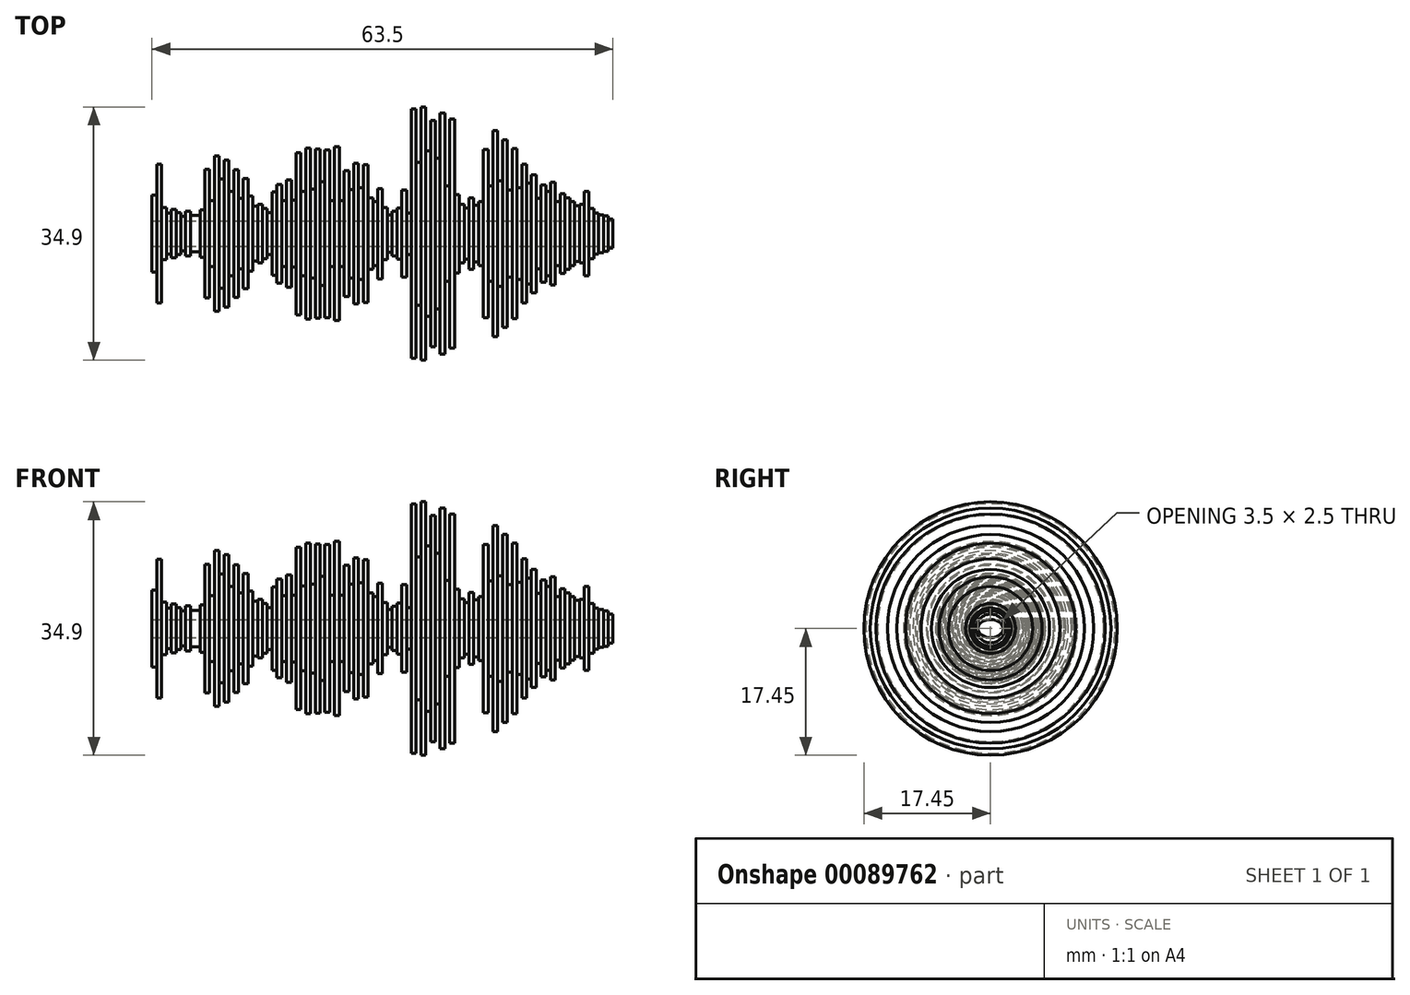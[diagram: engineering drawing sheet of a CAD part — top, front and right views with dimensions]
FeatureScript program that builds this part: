
annotation { "Feature Type Name" : "Feature", "Feature Type Description" : "" }
export const myFeature = defineFeature(function(context is Context, id is Id, definition is map)
    precondition{}
    {
        {
            var Q0;
            Q0=qCreatedBy(makeId("Front.planeOp"),FACE);
            var sketch = newSketch(context, id + "F0", { "sketchPlane" : qUnion([Q0])});
            skLineSegment(sketch, "E0", {"start": v(-31.75, 0) * mm, "end": v(31.75, 0) * mm});
            skLineSegment(sketch, "E1", {"start": v(-31.75, 0) * mm, "end": v(-31.75, 5.3) * mm});
            skLineSegment(sketch, "E2", {"start": v(-31.75, 5.3) * mm, "end": v(-31.09, 5.3) * mm});
            skLineSegment(sketch, "E3", {"start": v(-31.09, 9.56) * mm, "end": v(-30.43, 9.56) * mm});
            skLineSegment(sketch, "E4", {"start": v(-30.43, 3.61) * mm, "end": v(-29.77, 3.61) * mm});
            skLineSegment(sketch, "E5", {"start": v(-29.77, 2.8) * mm, "end": v(-29.1, 2.8) * mm});
            skLineSegment(sketch, "E6", {"start": v(-29.1, 3.36) * mm, "end": v(-28.44, 3.36) * mm});
            skLineSegment(sketch, "E7", {"start": v(-28.44, 2.9) * mm, "end": v(-27.78, 2.9) * mm});
            skLineSegment(sketch, "E8", {"start": v(-27.78, 2.4) * mm, "end": v(-27.12, 2.4) * mm});
            skLineSegment(sketch, "E9", {"start": v(-27.12, 3.1) * mm, "end": v(-26.46, 3.1) * mm});
            skLineSegment(sketch, "E10", {"start": v(-26.46, 2.52) * mm, "end": v(-25.8, 2.52) * mm});
            skLineSegment(sketch, "E11", {"start": v(-25.8, 2.52) * mm, "end": v(-25.14, 2.52) * mm});
            skLineSegment(sketch, "E12", {"start": v(-25.14, 3.27) * mm, "end": v(-24.47, 3.27) * mm});
            skLineSegment(sketch, "E13", {"start": v(-23.81, 4.52) * mm, "end": v(-23.15, 4.52) * mm});
            skLineSegment(sketch, "E14", {"start": v(-23.15, 10.72) * mm, "end": v(-22.49, 10.72) * mm});
            skLineSegment(sketch, "E15", {"start": v(-22.49, 7.5) * mm, "end": v(-21.83, 7.5) * mm});
            skLineSegment(sketch, "E16", {"start": v(-21.83, 10.16) * mm, "end": v(-21.17, 10.16) * mm});
            skLineSegment(sketch, "E17", {"start": v(-21.17, 5.8) * mm, "end": v(-20.5, 5.8) * mm});
            skLineSegment(sketch, "E18", {"start": v(-20.5, 8.8) * mm, "end": v(-19.84, 8.8) * mm});
            skLineSegment(sketch, "E19", {"start": v(-19.84, 4.88) * mm, "end": v(-19.18, 4.88) * mm});
            skLineSegment(sketch, "E20", {"start": v(-19.18, 7.6) * mm, "end": v(-18.52, 7.6) * mm});
            skLineSegment(sketch, "E21", {"start": v(-18.52, 5.19) * mm, "end": v(-17.86, 5.19) * mm});
            skLineSegment(sketch, "E22", {"start": v(-17.86, 3.79) * mm, "end": v(-17.2, 3.79) * mm});
            skLineSegment(sketch, "E23", {"start": v(-17.2, 4.02) * mm, "end": v(-16.54, 4.02) * mm});
            skLineSegment(sketch, "E24", {"start": v(-16.54, 3.44) * mm, "end": v(-15.88, 3.44) * mm});
            skLineSegment(sketch, "E25", {"start": v(-15.88, 2.87) * mm, "end": v(-15.21, 2.87) * mm});
            skLineSegment(sketch, "E26", {"start": v(-15.21, 5.73) * mm, "end": v(-14.55, 5.73) * mm});
            skLineSegment(sketch, "E27", {"start": v(-31.09, 5.3) * mm, "end": v(-31.09, 9.56) * mm});
            skLineSegment(sketch, "E28", {"start": v(-30.43, 9.56) * mm, "end": v(-30.43, 3.61) * mm});
            skLineSegment(sketch, "E29", {"start": v(-29.77, 3.61) * mm, "end": v(-29.77, 2.8) * mm});
            skLineSegment(sketch, "E30", {"start": v(-29.1, 3.36) * mm, "end": v(-29.1, 2.8) * mm});
            skLineSegment(sketch, "E31", {"start": v(-28.44, 3.36) * mm, "end": v(-28.44, 2.9) * mm});
            skLineSegment(sketch, "E32", {"start": v(-27.78, 2.9) * mm, "end": v(-27.78, 2.4) * mm});
            skLineSegment(sketch, "E33", {"start": v(-27.12, 2.4) * mm, "end": v(-27.12, 3.1) * mm});
            skLineSegment(sketch, "E34", {"start": v(-26.46, 3.1) * mm, "end": v(-26.46, 2.52) * mm});
            skLineSegment(sketch, "E35", {"start": v(-25.14, 2.52) * mm, "end": v(-25.14, 3.27) * mm});
            skLineSegment(sketch, "E36", {"start": v(-24.47, 3.27) * mm, "end": v(-24.47, 8.86) * mm});
            skLineSegment(sketch, "E37", {"start": v(-24.47, 8.86) * mm, "end": v(-23.81, 8.86) * mm});
            skLineSegment(sketch, "E38", {"start": v(-23.81, 8.86) * mm, "end": v(-23.81, 4.52) * mm});
            skLineSegment(sketch, "E39", {"start": v(-23.15, 4.52) * mm, "end": v(-23.15, 10.72) * mm});
            skLineSegment(sketch, "E40", {"start": v(-22.49, 10.72) * mm, "end": v(-22.49, 7.5) * mm});
            skLineSegment(sketch, "E41", {"start": v(-21.83, 7.5) * mm, "end": v(-21.83, 10.16) * mm});
            skLineSegment(sketch, "E42", {"start": v(-21.17, 10.16) * mm, "end": v(-21.17, 5.8) * mm});
            skLineSegment(sketch, "E43", {"start": v(-20.5, 5.8) * mm, "end": v(-20.5, 8.8) * mm});
            skLineSegment(sketch, "E44", {"start": v(-19.84, 8.8) * mm, "end": v(-19.84, 4.88) * mm});
            skLineSegment(sketch, "E45", {"start": v(-19.18, 4.88) * mm, "end": v(-19.18, 7.6) * mm});
            skLineSegment(sketch, "E46", {"start": v(-18.52, 7.6) * mm, "end": v(-18.52, 5.19) * mm});
            skLineSegment(sketch, "E47", {"start": v(-17.86, 3.79) * mm, "end": v(-17.86, 5.19) * mm});
            skLineSegment(sketch, "E48", {"start": v(-17.2, 4.02) * mm, "end": v(-17.2, 3.79) * mm});
            skLineSegment(sketch, "E49", {"start": v(-16.54, 3.44) * mm, "end": v(-16.54, 4.02) * mm});
            skLineSegment(sketch, "E50", {"start": v(-15.88, 3.44) * mm, "end": v(-15.88, 2.87) * mm});
            skLineSegment(sketch, "E51", {"start": v(-15.21, 2.87) * mm, "end": v(-15.21, 5.73) * mm});
            skLineSegment(sketch, "E52", {"start": v(-14.55, 6.8) * mm, "end": v(-14.55, 5.73) * mm});
            skLineSegment(sketch, "E53", {"start": v(-14.55, 6.8) * mm, "end": v(-13.9, 6.8) * mm});
            skLineSegment(sketch, "E54", {"start": v(-13.9, 4.56) * mm, "end": v(-13.23, 4.56) * mm});
            skLineSegment(sketch, "E55", {"start": v(-13.23, 7.4) * mm, "end": v(-12.57, 7.4) * mm});
            skLineSegment(sketch, "E56", {"start": v(-12.57, 4.59) * mm, "end": v(-11.9, 4.59) * mm});
            skLineSegment(sketch, "E57", {"start": v(-11.9, 11.17) * mm, "end": v(-11.24, 11.17) * mm});
            skLineSegment(sketch, "E58", {"start": v(-11.24, 5.84) * mm, "end": v(-10.58, 5.84) * mm});
            skLineSegment(sketch, "E59", {"start": v(-10.58, 11.76) * mm, "end": v(-9.92, 11.76) * mm});
            skLineSegment(sketch, "E60", {"start": v(-9.92, 6.14) * mm, "end": v(-9.26, 6.14) * mm});
            skLineSegment(sketch, "E61", {"start": v(-9.26, 11.66) * mm, "end": v(-8.6, 11.66) * mm});
            skLineSegment(sketch, "E62", {"start": v(-8.6, 7.17) * mm, "end": v(-7.94, 7.17) * mm});
            skLineSegment(sketch, "E63", {"start": v(-7.94, 11.56) * mm, "end": v(-7.28, 11.56) * mm});
            skLineSegment(sketch, "E64", {"start": v(-7.28, 4.56) * mm, "end": v(-6.61, 4.56) * mm});
            skLineSegment(sketch, "E65", {"start": v(-6.61, 12) * mm, "end": v(-5.95, 12) * mm});
            skLineSegment(sketch, "E66", {"start": v(-5.95, 4.56) * mm, "end": v(-5.3, 4.56) * mm});
            skLineSegment(sketch, "E67", {"start": v(-13.9, 6.8) * mm, "end": v(-13.9, 4.56) * mm});
            skLineSegment(sketch, "E68", {"start": v(-13.23, 7.4) * mm, "end": v(-13.23, 4.56) * mm});
            skLineSegment(sketch, "E69", {"start": v(-12.57, 7.4) * mm, "end": v(-12.57, 4.59) * mm});
            skLineSegment(sketch, "E70", {"start": v(-11.9, 11.17) * mm, "end": v(-11.9, 4.59) * mm});
            skLineSegment(sketch, "E71", {"start": v(-11.24, 11.17) * mm, "end": v(-11.24, 5.84) * mm});
            skLineSegment(sketch, "E72", {"start": v(-10.58, 11.76) * mm, "end": v(-10.58, 5.84) * mm});
            skLineSegment(sketch, "E73", {"start": v(-9.92, 11.76) * mm, "end": v(-9.92, 6.14) * mm});
            skLineSegment(sketch, "E74", {"start": v(-9.26, 11.66) * mm, "end": v(-9.26, 6.14) * mm});
            skLineSegment(sketch, "E75", {"start": v(-8.6, 11.66) * mm, "end": v(-8.6, 7.17) * mm});
            skLineSegment(sketch, "E76", {"start": v(-7.94, 11.56) * mm, "end": v(-7.94, 7.17) * mm});
            skLineSegment(sketch, "E77", {"start": v(-7.28, 11.56) * mm, "end": v(-7.28, 4.56) * mm});
            skLineSegment(sketch, "E78", {"start": v(-6.61, 4.56) * mm, "end": v(-6.61, 12) * mm});
            skLineSegment(sketch, "E79", {"start": v(-5.95, 12) * mm, "end": v(-5.95, 4.56) * mm});
            skLineSegment(sketch, "E80", {"start": v(-5.3, 8.69) * mm, "end": v(-4.63, 8.69) * mm});
            skLineSegment(sketch, "E81", {"start": v(-4.63, 6.1) * mm, "end": v(-3.97, 6.1) * mm});
            skLineSegment(sketch, "E82", {"start": v(-3.97, 9.7) * mm, "end": v(-3.3, 9.7) * mm});
            skLineSegment(sketch, "E83", {"start": v(-3.3, 6.33) * mm, "end": v(-2.65, 6.33) * mm});
            skLineSegment(sketch, "E84", {"start": v(-2.65, 9.47) * mm, "end": v(-1.98, 9.47) * mm});
            skLineSegment(sketch, "E85", {"start": v(-1.98, 4.9) * mm, "end": v(-1.32, 4.9) * mm});
            skLineSegment(sketch, "E86", {"start": v(-1.32, 4.4) * mm, "end": v(-0.66, 4.4) * mm});
            skLineSegment(sketch, "E87", {"start": v(-0.66, 6.23) * mm, "end": v(0, 6.23) * mm});
            skLineSegment(sketch, "E88", {"start": v(0, 3.6) * mm, "end": v(0.66, 3.6) * mm});
            skLineSegment(sketch, "E89", {"start": v(0.66, 2.6) * mm, "end": v(1.32, 2.6) * mm});
            skLineSegment(sketch, "E90", {"start": v(1.32, 3.06) * mm, "end": v(1.98, 3.06) * mm});
            skLineSegment(sketch, "E91", {"start": v(1.98, 3.53) * mm, "end": v(2.65, 3.53) * mm});
            skLineSegment(sketch, "E92", {"start": v(2.65, 6.02) * mm, "end": v(3.3, 6.02) * mm});
            skLineSegment(sketch, "E93", {"start": v(3.3, 2.86) * mm, "end": v(3.97, 2.86) * mm});
            skLineSegment(sketch, "E94", {"start": v(3.97, 17.17) * mm, "end": v(4.63, 17.17) * mm});
            skLineSegment(sketch, "E95", {"start": v(4.63, 9.84) * mm, "end": v(5.3, 9.84) * mm});
            skLineSegment(sketch, "E96", {"start": v(5.3, 17.45) * mm, "end": v(5.95, 17.45) * mm});
            skLineSegment(sketch, "E97", {"start": v(5.95, 11.39) * mm, "end": v(6.61, 11.39) * mm});
            skLineSegment(sketch, "E98", {"start": v(6.61, 15.58) * mm, "end": v(7.28, 15.58) * mm});
            skLineSegment(sketch, "E99", {"start": v(7.28, 10.37) * mm, "end": v(7.94, 10.37) * mm});
            skLineSegment(sketch, "E100", {"start": v(7.94, 16.59) * mm, "end": v(8.6, 16.59) * mm});
            skLineSegment(sketch, "E101", {"start": v(8.6, 6.6) * mm, "end": v(9.26, 6.6) * mm});
            skLineSegment(sketch, "E102", {"start": v(9.26, 15.79) * mm, "end": v(9.92, 15.79) * mm});
            skLineSegment(sketch, "E103", {"start": v(9.92, 5.4) * mm, "end": v(10.58, 5.4) * mm});
            skLineSegment(sketch, "E104", {"start": v(10.58, 4.06) * mm, "end": v(11.24, 4.06) * mm});
            skLineSegment(sketch, "E105", {"start": v(11.24, 3.55) * mm, "end": v(11.9, 3.55) * mm});
            skLineSegment(sketch, "E106", {"start": v(11.9, 4.95) * mm, "end": v(12.57, 4.95) * mm});
            skLineSegment(sketch, "E107", {"start": v(12.57, 3.93) * mm, "end": v(13.23, 3.93) * mm});
            skLineSegment(sketch, "E108", {"start": v(13.23, 4.4) * mm, "end": v(13.9, 4.4) * mm});
            skLineSegment(sketch, "E109", {"start": v(13.9, 11.6) * mm, "end": v(14.55, 11.6) * mm});
            skLineSegment(sketch, "E110", {"start": v(14.55, 6.56) * mm, "end": v(15.21, 6.56) * mm});
            skLineSegment(sketch, "E111", {"start": v(15.21, 14.2) * mm, "end": v(15.88, 14.2) * mm});
            skLineSegment(sketch, "E112", {"start": v(-4.63, 6.1) * mm, "end": v(-4.63, 8.69) * mm});
            skLineSegment(sketch, "E113", {"start": v(-3.97, 9.7) * mm, "end": v(-3.97, 6.1) * mm});
            skLineSegment(sketch, "E114", {"start": v(-3.3, 9.7) * mm, "end": v(-3.3, 6.33) * mm});
            skLineSegment(sketch, "E115", {"start": v(-2.65, 9.47) * mm, "end": v(-2.65, 6.33) * mm});
            skLineSegment(sketch, "E116", {"start": v(-1.98, 4.9) * mm, "end": v(-1.98, 9.47) * mm});
            skLineSegment(sketch, "E117", {"start": v(-1.32, 4.4) * mm, "end": v(-1.32, 4.9) * mm});
            skLineSegment(sketch, "E118", {"start": v(-0.66, 4.4) * mm, "end": v(-0.66, 6.23) * mm});
            skLineSegment(sketch, "E119", {"start": v(0, 6.23) * mm, "end": v(0, 3.6) * mm});
            skLineSegment(sketch, "E120", {"start": v(0.66, 2.6) * mm, "end": v(0.66, 3.6) * mm});
            skLineSegment(sketch, "E121", {"start": v(1.32, 2.6) * mm, "end": v(1.32, 3.06) * mm});
            skLineSegment(sketch, "E122", {"start": v(1.98, 3.06) * mm, "end": v(1.98, 3.53) * mm});
            skLineSegment(sketch, "E123", {"start": v(2.65, 3.53) * mm, "end": v(2.65, 6.02) * mm});
            skLineSegment(sketch, "E124", {"start": v(3.3, 2.86) * mm, "end": v(3.3, 6.02) * mm});
            skLineSegment(sketch, "E125", {"start": v(3.97, 2.86) * mm, "end": v(3.97, 17.17) * mm});
            skLineSegment(sketch, "E126", {"start": v(4.63, 9.84) * mm, "end": v(4.63, 17.17) * mm});
            skLineSegment(sketch, "E127", {"start": v(5.3, 9.84) * mm, "end": v(5.3, 17.45) * mm});
            skLineSegment(sketch, "E128", {"start": v(5.95, 11.39) * mm, "end": v(5.95, 17.45) * mm});
            skLineSegment(sketch, "E129", {"start": v(7.28, 10.37) * mm, "end": v(7.28, 15.58) * mm});
            skLineSegment(sketch, "E130", {"start": v(7.94, 10.37) * mm, "end": v(7.94, 16.59) * mm});
            skLineSegment(sketch, "E131", {"start": v(8.6, 6.6) * mm, "end": v(8.6, 16.59) * mm});
            skLineSegment(sketch, "E132", {"start": v(9.26, 15.79) * mm, "end": v(9.26, 6.6) * mm});
            skLineSegment(sketch, "E133", {"start": v(9.92, 15.79) * mm, "end": v(9.92, 5.4) * mm});
            skLineSegment(sketch, "E134", {"start": v(11.24, 3.55) * mm, "end": v(11.24, 4.06) * mm});
            skLineSegment(sketch, "E135", {"start": v(11.9, 3.55) * mm, "end": v(11.9, 4.95) * mm});
            skLineSegment(sketch, "E136", {"start": v(12.57, 3.93) * mm, "end": v(12.57, 4.95) * mm});
            skLineSegment(sketch, "E137", {"start": v(13.23, 3.93) * mm, "end": v(13.23, 4.4) * mm});
            skLineSegment(sketch, "E138", {"start": v(13.9, 4.4) * mm, "end": v(13.9, 11.6) * mm});
            skLineSegment(sketch, "E139", {"start": v(14.55, 6.56) * mm, "end": v(14.55, 11.6) * mm});
            skLineSegment(sketch, "E140", {"start": v(15.21, 6.56) * mm, "end": v(15.21, 14.2) * mm});
            skLineSegment(sketch, "E141", {"start": v(15.88, 7.28) * mm, "end": v(16.54, 7.28) * mm});
            skLineSegment(sketch, "E142", {"start": v(16.54, 12.94) * mm, "end": v(17.2, 12.94) * mm});
            skLineSegment(sketch, "E143", {"start": v(17.2, 6.02) * mm, "end": v(17.86, 6.02) * mm});
            skLineSegment(sketch, "E144", {"start": v(17.86, 11.74) * mm, "end": v(18.52, 11.74) * mm});
            skLineSegment(sketch, "E145", {"start": v(18.52, 6.34) * mm, "end": v(19.18, 6.34) * mm});
            skLineSegment(sketch, "E146", {"start": v(19.18, 9.58) * mm, "end": v(19.84, 9.58) * mm});
            skLineSegment(sketch, "E147", {"start": v(19.84, 6.94) * mm, "end": v(20.5, 6.94) * mm});
            skLineSegment(sketch, "E148", {"start": v(20.5, 8.12) * mm, "end": v(21.17, 8.12) * mm});
            skLineSegment(sketch, "E149", {"start": v(21.17, 4.83) * mm, "end": v(21.83, 4.83) * mm});
            skLineSegment(sketch, "E150", {"start": v(21.83, 6.67) * mm, "end": v(22.49, 6.67) * mm});
            skLineSegment(sketch, "E151", {"start": v(22.49, 5.8) * mm, "end": v(23.15, 5.8) * mm});
            skLineSegment(sketch, "E152", {"start": v(23.15, 7.1) * mm, "end": v(23.81, 7.1) * mm});
            skLineSegment(sketch, "E153", {"start": v(23.81, 4.39) * mm, "end": v(24.47, 4.39) * mm});
            skLineSegment(sketch, "E154", {"start": v(24.47, 5.47) * mm, "end": v(25.14, 5.47) * mm});
            skLineSegment(sketch, "E155", {"start": v(25.14, 4.9) * mm, "end": v(25.8, 4.9) * mm});
            skLineSegment(sketch, "E156", {"start": v(25.8, 4.39) * mm, "end": v(26.46, 4.39) * mm});
            skLineSegment(sketch, "E157", {"start": v(26.46, 3.87) * mm, "end": v(27.12, 3.87) * mm});
            skLineSegment(sketch, "E158", {"start": v(27.12, 4.03) * mm, "end": v(27.78, 4.03) * mm});
            skLineSegment(sketch, "E159", {"start": v(27.78, 5.8) * mm, "end": v(28.44, 5.8) * mm});
            skLineSegment(sketch, "E160", {"start": v(28.44, 3.43) * mm, "end": v(29.1, 3.43) * mm});
            skLineSegment(sketch, "E161", {"start": v(29.1, 2.83) * mm, "end": v(29.77, 2.83) * mm});
            skLineSegment(sketch, "E162", {"start": v(29.77, 2.6) * mm, "end": v(30.43, 2.6) * mm});
            skLineSegment(sketch, "E163", {"start": v(30.43, 2.45) * mm, "end": v(31.09, 2.45) * mm});
            skLineSegment(sketch, "E164", {"start": v(31.09, 1.99) * mm, "end": v(31.75, 1.99) * mm});
            skLineSegment(sketch, "E165", {"start": v(16.54, 7.28) * mm, "end": v(16.54, 12.94) * mm});
            skLineSegment(sketch, "E166", {"start": v(17.2, 12.94) * mm, "end": v(17.2, 6.02) * mm});
            skLineSegment(sketch, "E167", {"start": v(17.86, 11.74) * mm, "end": v(17.86, 6.02) * mm});
            skLineSegment(sketch, "E168", {"start": v(18.52, 11.74) * mm, "end": v(18.52, 6.34) * mm});
            skLineSegment(sketch, "E169", {"start": v(19.18, 6.34) * mm, "end": v(19.18, 9.58) * mm});
            skLineSegment(sketch, "E170", {"start": v(19.84, 6.94) * mm, "end": v(19.84, 9.58) * mm});
            skLineSegment(sketch, "E171", {"start": v(21.17, 8.12) * mm, "end": v(21.17, 4.83) * mm});
            skLineSegment(sketch, "E172", {"start": v(21.83, 4.83) * mm, "end": v(21.83, 6.67) * mm});
            skLineSegment(sketch, "E173", {"start": v(22.49, 5.8) * mm, "end": v(22.49, 6.67) * mm});
            skLineSegment(sketch, "E174", {"start": v(23.15, 5.8) * mm, "end": v(23.15, 7.1) * mm});
            skLineSegment(sketch, "E175", {"start": v(23.81, 4.39) * mm, "end": v(23.81, 7.1) * mm});
            skLineSegment(sketch, "E176", {"start": v(24.47, 4.39) * mm, "end": v(24.47, 5.47) * mm});
            skLineSegment(sketch, "E177", {"start": v(25.14, 4.9) * mm, "end": v(25.14, 5.47) * mm});
            skLineSegment(sketch, "E178", {"start": v(25.8, 4.39) * mm, "end": v(25.8, 4.9) * mm});
            skLineSegment(sketch, "E179", {"start": v(26.46, 3.87) * mm, "end": v(26.46, 4.39) * mm});
            skLineSegment(sketch, "E180", {"start": v(27.12, 3.87) * mm, "end": v(27.12, 4.03) * mm});
            skLineSegment(sketch, "E181", {"start": v(27.78, 4.03) * mm, "end": v(27.78, 5.8) * mm});
            skLineSegment(sketch, "E182", {"start": v(28.44, 3.43) * mm, "end": v(28.44, 5.8) * mm});
            skLineSegment(sketch, "E183", {"start": v(29.1, 2.83) * mm, "end": v(29.1, 3.43) * mm});
            skLineSegment(sketch, "E184", {"start": v(29.77, 2.6) * mm, "end": v(29.77, 2.83) * mm});
            skLineSegment(sketch, "E185", {"start": v(30.43, 2.6) * mm, "end": v(30.43, 2.45) * mm});
            skLineSegment(sketch, "E186", {"start": v(31.09, 2.45) * mm, "end": v(31.09, 1.99) * mm});
            skLineSegment(sketch, "E187", {"start": v(31.75, 1.99) * mm, "end": v(31.75, 0) * mm});
            skLineSegment(sketch, "E188", {"start": v(15.88, 14.2) * mm, "end": v(15.88, 7.28) * mm});
            skLineSegment(sketch, "E189", {"start": v(-5.3, 4.56) * mm, "end": v(-5.3, 8.69) * mm});
            skLineSegment(sketch, "E190", {"start": v(6.61, 11.39) * mm, "end": v(6.61, 15.58) * mm});
            skLineSegment(sketch, "E191", {"start": v(10.58, 5.4) * mm, "end": v(10.58, 4.06) * mm});
            skLineSegment(sketch, "E192", {"start": v(20.5, 8.12) * mm, "end": v(20.5, 6.94) * mm});
            skSolve(sketch);
        }
        {
            var Q0;
            Q0=makeQuery(id+"F0.imprint","IMPRINT",FACE,{"disambiguationData":[TD([[makeQuery(id+"F0.imprint","IMPRINT",EDGE,{"derivedFrom":sQuery(id+"F0.wireOp",EDGE,"E0")}),1.0]])]});
            var Q1;
            Q1=sQuery(id+"F0.wireOp",EDGE,"E0");
            revolve(context, id + "F1", {"entities" : qUnion([Q0]), "axis" : qUnion([Q1]), "revolveType" : RevolveType.FULL});
        }
        {
            var Q0;
            Q0=makeQuery(id+"F1.opRevolve","SWEPT_FACE",FACE,{"disambiguationData":[OSD([sQuery(id+"F0.wireOp",EDGE,"E187")])]});
            var sketch = newSketch(context, id + "F2", { "sketchPlane" : qUnion([Q0])});
            skEllipse(sketch, "E193", {"center": v(0, 0) * mm, "majorRadius": 1.75 * mm, "minorRadius": 1.25 * mm, "majorAxis": v(1, 0)});
            skLineSegment(sketch, "E194", {"start": v(-1.75, 0) * mm, "end": v(1.75, 0) * mm, "construction": true});
            skLineSegment(sketch, "E195", {"start": v(0, 1.25) * mm, "end": v(0, -1.25) * mm, "construction": true});
            skSolve(sketch);
        }
        {
            var Q0;
            Q0=makeQuery(id+"F2.imprint","IMPRINT",FACE,{"disambiguationData":[TD([[makeQuery(id+"F2.imprint","IMPRINT",EDGE,{"derivedFrom":sQuery(id+"F2.wireOp",EDGE,"E193")}),1.0]])]});
            extrude(context, id + "F3", {"entities" : qUnion([Q0]), "operationType" : NewBodyOperationType.REMOVE, "endBound" : BoundingType.THROUGH_ALL, "oppositeDirection" : true, "depth" : 25.4 * mm});
        }
    });
